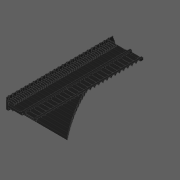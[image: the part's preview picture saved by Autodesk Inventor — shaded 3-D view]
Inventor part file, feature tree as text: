
AUTODESK INVENTOR PART (.ipt)
format: ipt  version: 2020 (Build 240168000, 168)  size: 4,580,864 bytes
history: native  units: in
note: dims shown in document units (in); Inventor stores cm internally (conversion verified against a paired STEP export)
features: other x37, extrude x21, loft x3, pattern_linear x3, fillet x2, sketch x1, projected_geometry x1
ambient origin geometry x8: Origin, YZ Plane, XZ Plane, XY Plane, X Axis, Y Axis, Z Axis, Center Point
bodies: Body1 (feature_tree), Body2 (feature_tree)
feature tree (68):
  other  "CrossSection1"
  other  "CrossSection2"
  other  "CrossSection3"
  other  "Whole"
  other  "Vertical Midplane"
  other  "Horizontal Midplane"
  extrude  "Block"  Depth=0.0197in
  extrude  "Hinge Protrusion"  Depth=0.0197in
  other  "Resonator Profile"
  extrude  "Resonator"  Depth=0.0197in
  extrude  "Resonator Cut"  TaperAngle=0.0deg  [1 undecoded]
  extrude  "Duct Cavity"  Depth=0.4882in
  other  "Duct Cavity Plane"
  loft  "Duct Entrance Loft"
  other  "Whistle Path Midplane"
  other  "Slit Loft To"
  loft  "Slit Loft"
  extrude  "Slit"  TaperAngle=0.0deg  [1 undecoded]
  other  "Fitting"
  extrude  "Edge Cut"  Depth=0.0197in
  other  "Edge Plane"
  other  "Edge Sketch"
  loft  "Edge Loft"
  extrude  "Edge"  TaperAngle=90.0deg  [1 undecoded]
  other  "Edge Cut Plane"
  extrude  "Spring Steel Slot"  Depth=0.0197in
  fillet  "Duct Fillet"  [1 undecoded]
  pattern_linear  "Channel Repetition"  Spacing1=0.2441in  [1 undecoded]
  extrude  "Edge Length Cut"  Depth=0.0197in
  other  "Tube Length Curve"
  extrude  "Long Tubes Length Cut"  Depth=0.0197in
  extrude  "Short Tubes Length Cut"  Depth=0.0197in
  extrude  "Whistle Walls"  Depth=0.0197in
  fillet  "Whistle Wall Fillet"  Radius=0.4921in
  pattern_linear  "Whistle Wall Repetition"  Spacing1=0.0197in  [1 undecoded]
  extrude  "End Caps"  Depth=0.2559in
  extrude  "Extra Block (for short notes)"  Depth=0.0197in
  other  "End Cap Tidying Plane"
  other  "End Cap Tidying Sketch"
  extrude  "End Cap Tidying"  Depth=0.4882in
  extrude  "End Cap Tidying (reverse)"  TaperAngle=0.0deg  [1 undecoded]
  pattern_linear  "End Cap Tidying Repetition"  Spacing1=0.2441in  [1 undecoded]
  extrude  "End Cap Tidying (edges)"  Depth=0.0197in
  extrude  "End Cap Tidying (edges, reverse)"  Depth=0.0197in
  other  "End-of-block Plane"
  extrude  "Manifold Slots"  Depth=0.0197in
  extrude  "Extension for Top C Key"  TaperAngle=0.0deg  [1 undecoded]
  other  "Split Plane"
  other  "Split for Printing"
  other  "Block Profile"
  other  "Fitting Sketch"
  other  "Duct Cavity Profile"
  other  "Duct Entrance Loft From"
  other  "Hinge Protrusion Sketch"
  other  "Edge Cut Sketch"
  other  "Edges3"
  other  "Edge Length Curve"
  other  "Whistle Wall Sketch"
  other  "2D Equation Curve10"
  other  "2D Equation Curve11"
  other  "Duct Entrance Loft To"
  other  "Slit Loft From"
  other  "Manifold Slot Sketch"
  other  "Spring Steel Slot Sketch"
  sketch  "Sketch27"  dims[d6=0.0in d7=9.8425in d9=0.4724in d20=0.3153in d21=0.0in d58=0.4882in d59=0.0in d62=2.3498in d63=0.0in d70=0.1969in d71=0.1292in d80=90.0deg d105=0.2362in d106=0.0in d109=0.2441in d111=0.1528in d112=0.1245in d114=0.1528in d115=0.2441in d118=0.4921in d148=0.0197in d150=0.2559in d151=0.8819in d152=0.4882in d154=0.0in d162=0.2441in d163=0.2362in d165=0.2441in d166=0.2461in d167=0.0in d171=0.2362in d174=0.4882in d175=0.4567in d176=0.0in d177=90.0deg d178=0.0in d179=90.0deg d185=0.3788in d186=0.0in d189=0.1954in d190=28.3465in d191=38.2021in d198=0.0803in d199=0.0in d200=0.0197in d201=0.0787in d202=-0.125in d203=0.7874in d206=0.2559in d209=0.0in d211=9.8425in d213=0.4724in d214=0.2362in d216=0.4567in d217=0.4882in d223=1.5748in d229=0.4882in d230=0.0in d234=0.4724in d235=0.4882in d237=0.2441in d239=1.4483in d240=0.0in d241=9.8425in d243=0.4724in d246=0.0394in d247=0.7043in d248=0.0in d249=0.2441in d250=11.8189in d251=0.0079in d252=28.3465in d253=38.2021in d254=28.3465in d255=38.2021in d256=-0.1575in d257=0.2362in d258=0.2151in d259=0.2441in d261=0.0in d262=90.0deg d263=0.0in d264=90.0deg d265=11.8268in d266=6.7754in d269=0.9992in d270=0.0in d271=0.9992in d272=0.0in d276=0.4882in d277=0.4567in d278=0.4882in d279=0.1954in d280=3.2088in d283=0.2362in d284=0.2441in d285=0.4486in d286=0.5118in d287=0.0in d288=90.0deg d289=0.0in d290=90.0deg d292=0.4882in d293=0.0in d294=1.5748in d295=0.4803in d299=0.5906in d300=0.0in d319=0.1299in d320=0.0787in d321=0.0669in d325=0.1299in d326=0.0787in d327=0.0669in d331=0.1299in d332=0.0787in d333=0.0669in d334=0.1299in d335=0.0787in d336=0.0669in d343=1.8898in d344=1.8898in d345=0.9449in d346=1.4173in d347=0.1299in d348=0.0787in d349=0.0669in d350=0.1299in d351=0.0787in d352=0.0669in d359=1.8898in d375=0.9449in d376=0.1299in d377=0.0787in d378=0.0669in d382=1.8898in d388=0.0317in d389=0.2559in d392=0.2072in d393=0.0in d396=0.2899in d397=0.0197in d398=0.0787in d399=0.0in d400=0.7874in d403=0.0618in d405=0.0197in d406=0.0787in d407=0.0in d408=0.7874in d410=0.1102in d411=0.0in d413=0.1969in d416=0.1095in d417=0.1575in d419=0.4882in d432=0.1412in d434=0.1875in d440=0.2441in d441=0.0in d442=1.5748in d443=0.0157in d444=45.0deg d445=0.4882in d448=0.2441in d451=0.1181in d452=0.5906in d453=0.1969in d457=0.122in d461=0.286in d462=0.0in d137=0.0197in d138=0.0344in d139=0.0197in d140=0.0344in d207=0.0344in d208=0.0197in d267=0.0197in d268=0.0344in d281=0.0197in d282=0.0344in d414=0.0344in d415=0.0197in d425=0.0197in d426=0.0344in d427=0.0197in d428=0.0344in]
  projected_geometry  "Projected Loop5"
  other  "Upper"
  other  "Lower"
note: 9 required parameter values undecoded (feature->parameter linkage not recoverable at this tier; creation-order binding heuristic only, values carry confidence <= 0.55)
